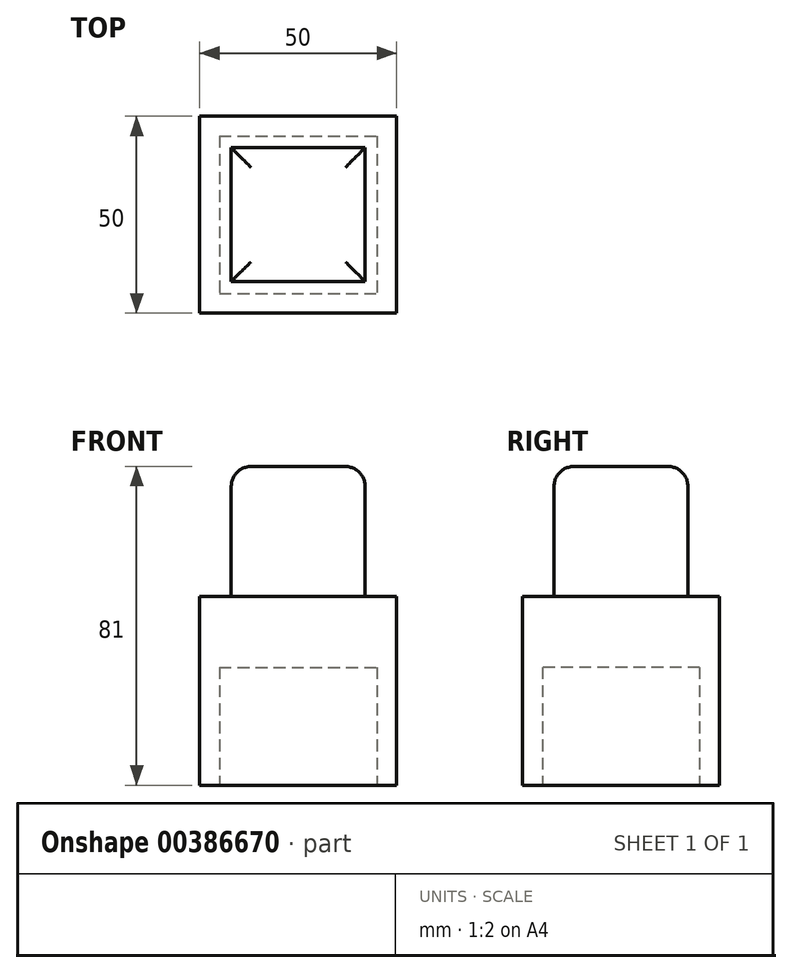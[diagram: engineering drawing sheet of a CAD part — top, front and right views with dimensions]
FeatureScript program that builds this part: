
annotation { "Feature Type Name" : "Feature", "Feature Type Description" : "" }
export const myFeature = defineFeature(function(context is Context, id is Id, definition is map)
    precondition{}
    {
        {
            var Q0;
            Q0=qCreatedBy(makeId("Top.planeOp"),FACE);
            var sketch = newSketch(context, id + "F0", { "sketchPlane" : qUnion([Q0])});
            skLineSegment(sketch, "E0.bottom", {"start": v(0, 0) * mm, "end": v(50, 0) * mm});
            skLineSegment(sketch, "E0.top", {"start": v(0, 50) * mm, "end": v(50, 50) * mm});
            skLineSegment(sketch, "E0.left", {"start": v(0, 0) * mm, "end": v(0, 50) * mm});
            skLineSegment(sketch, "E0.right", {"start": v(50, 0) * mm, "end": v(50, 50) * mm});
            skLineSegment(sketch, "E1.bottom", {"start": v(5, 45) * mm, "end": v(45, 45) * mm});
            skLineSegment(sketch, "E1.top", {"start": v(5, 5) * mm, "end": v(45, 5) * mm});
            skLineSegment(sketch, "E1.left", {"start": v(5, 45) * mm, "end": v(5, 5) * mm});
            skLineSegment(sketch, "E1.right", {"start": v(45, 45) * mm, "end": v(45, 5) * mm});
            skPoint(sketch, "E1.middle", {"position": v(25, 25) * mm});
            skLineSegment(sketch, "E2", {"start": v(25, 25) * mm, "end": v(25, 50) * mm, "construction": true});
            skLineSegment(sketch, "E3", {"start": v(25, 25) * mm, "end": v(0, 25) * mm, "construction": true});
            skSolve(sketch);
        }
        {
            var Q0;
            Q0 = qSketchRegion(id + "F0", true);
            extrude(context, id + "F1", {"entities" : qUnion([Q0]), "depth" : 30 * mm});
        }
        {
            var Q0;
            Q0=makeQuery(id+"F1.opExtrude","CAP_FACE",FACE,{"disambiguationData":[OSD([sQuery(id+"F0.wireOp",EDGE,"E0.bottom"),sQuery(id+"F0.wireOp",EDGE,"E0.top"),sQuery(id+"F0.wireOp",EDGE,"E0.left"),sQuery(id+"F0.wireOp",EDGE,"E0.right"),sQuery(id+"F0.wireOp",EDGE,"E1.bottom"),sQuery(id+"F0.wireOp",EDGE,"E1.top"),sQuery(id+"F0.wireOp",EDGE,"E1.left"),sQuery(id+"F0.wireOp",EDGE,"E1.right")])],"isStart":false});
            var sketch = newSketch(context, id + "F2", { "sketchPlane" : qUnion([Q0])});
            skLineSegment(sketch, "E4.bottom", {"start": v(0, 50) * mm, "end": v(50, 50) * mm});
            skLineSegment(sketch, "E4.top", {"start": v(0, 0) * mm, "end": v(50, 0) * mm});
            skLineSegment(sketch, "E4.left", {"start": v(0, 50) * mm, "end": v(0, 0) * mm});
            skLineSegment(sketch, "E4.right", {"start": v(50, 50) * mm, "end": v(50, 0) * mm});
            skSolve(sketch);
        }
        {
            var Q0;
            Q0 = qSketchRegion(id + "F2", true);
            extrude(context, id + "F3", {"entities" : qUnion([Q0]), "operationType" : NewBodyOperationType.ADD, "depth" : 18 * mm});
        }
        {
            var Q0;
            Q0=makeQuery(id+"F3.opExtrude","CAP_FACE",FACE,{"disambiguationData":[OSD([sQuery(id+"F2.wireOp",EDGE,"E4.bottom"),sQuery(id+"F2.wireOp",EDGE,"E4.top"),sQuery(id+"F2.wireOp",EDGE,"E4.left"),sQuery(id+"F2.wireOp",EDGE,"E4.right")])],"isStart":false});
            var sketch = newSketch(context, id + "F4", { "sketchPlane" : qUnion([Q0])});
            skLineSegment(sketch, "E5.0", {"start": v(8, 8) * mm, "end": v(8, 42) * mm});
            skLineSegment(sketch, "E5.1", {"start": v(8, 8) * mm, "end": v(42, 8) * mm});
            skLineSegment(sketch, "E5.2", {"start": v(42, 8) * mm, "end": v(42, 42) * mm});
            skLineSegment(sketch, "E5.3", {"start": v(8, 42) * mm, "end": v(42, 42) * mm});
            skSolve(sketch);
        }
        {
            var Q0;
            Q0 = qSketchRegion(id + "F4", true);
            extrude(context, id + "F5", {"entities" : qUnion([Q0]), "operationType" : NewBodyOperationType.ADD, "depth" : 33 * mm});
        }
        {
            var Q0;
            Q0=makeQuery(id+"F5.opExtrude","CAP_EDGE",EDGE,{"disambiguationData":[OSD([sQuery(id+"F4.wireOp",EDGE,"E5.1")])],"isStart":false});
            var Q1;
            Q1=makeQuery(id+"F5.opExtrude","CAP_EDGE",EDGE,{"disambiguationData":[OSD([sQuery(id+"F4.wireOp",EDGE,"E5.0")])],"isStart":false});
            var Q2;
            Q2=makeQuery(id+"F5.opExtrude","CAP_EDGE",EDGE,{"disambiguationData":[OSD([sQuery(id+"F4.wireOp",EDGE,"E5.3")])],"isStart":false});
            var Q3;
            Q3=makeQuery(id+"F5.opExtrude","CAP_EDGE",EDGE,{"disambiguationData":[OSD([sQuery(id+"F4.wireOp",EDGE,"E5.2")])],"isStart":false});
            fillet(context, id + "F6", {"entities" : qUnion([Q0, Q1, Q2, Q3]), "radius" : 5 * mm, "tangentPropagation" : true, "allowEdgeOverflow" : false});
        }
    });
